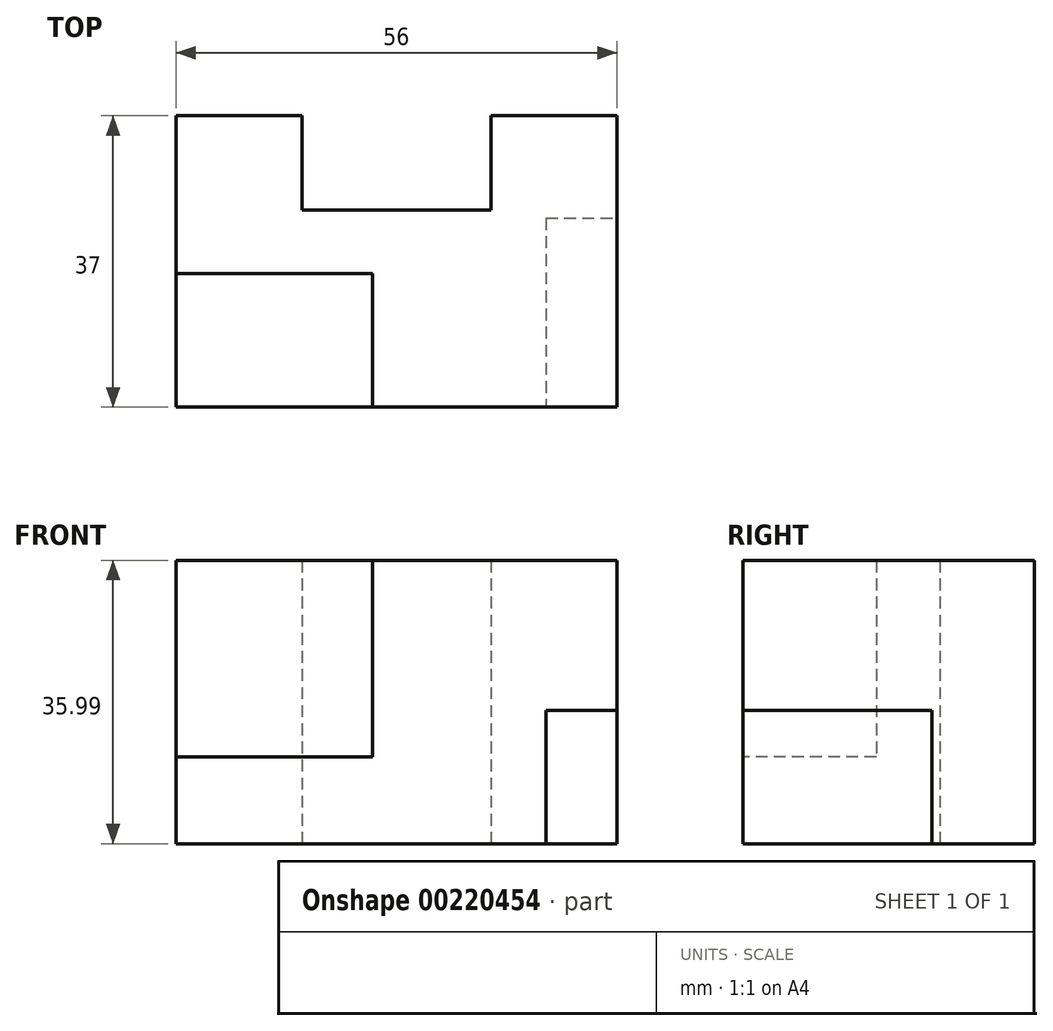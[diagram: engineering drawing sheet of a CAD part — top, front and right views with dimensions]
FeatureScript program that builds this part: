
annotation { "Feature Type Name" : "Feature", "Feature Type Description" : "" }
export const myFeature = defineFeature(function(context is Context, id is Id, definition is map)
    precondition{}
    {
        {
            var Q0;
            Q0=qCreatedBy(makeId("Top.planeOp"),FACE);
            var sketch = newSketch(context, id + "F0", { "sketchPlane" : qUnion([Q0])});
            skLineSegment(sketch, "E0.bottom", {"start": v(28, 18.5) * mm, "end": v(12, 18.5) * mm});
            skLineSegment(sketch, "E0.top", {"start": v(28, -18.5) * mm, "end": v(-28, -18.5) * mm});
            skLineSegment(sketch, "E0.left", {"start": v(28, 18.5) * mm, "end": v(28, -18.5) * mm});
            skLineSegment(sketch, "E0.right", {"start": v(-28, 18.5) * mm, "end": v(-28, -18.5) * mm});
            skPoint(sketch, "E0.middle", {"position": v(0, 0) * mm});
            skLineSegment(sketch, "E1.0", {"start": v(12, 18.5) * mm, "end": v(12, 6.52) * mm});
            skLineSegment(sketch, "E2.0", {"start": v(12, 6.52) * mm, "end": v(-12, 6.52) * mm});
            skLineSegment(sketch, "E3.0", {"start": v(-12, 18.5) * mm, "end": v(-12, 6.52) * mm});
            skLineSegment(sketch, "E4.trimOffspring", {"start": v(-12, 18.5) * mm, "end": v(-28, 18.5) * mm});
            skSolve(sketch);
        }
        {
            var Q0;
            Q0=makeQuery(id+"F0.imprint","IMPRINT",FACE,{"disambiguationData":[TD([[makeQuery(id+"F0.imprint","IMPRINT",EDGE,{"derivedFrom":sQuery(id+"F0.wireOp",EDGE,"E0.bottom")}),1.0]])]});
            extrude(context, id + "F1", {"entities" : qUnion([Q0]), "depth" : 36 * mm});
        }
        {
            var Q0;
            Q0=makeQuery(id+"F1.opExtrude","SWEPT_FACE",FACE,{"disambiguationData":[OSD([sQuery(id+"F0.wireOp",EDGE,"E0.left")])]});
            var sketch = newSketch(context, id + "F2", { "sketchPlane" : qUnion([Q0])});
            skLineSegment(sketch, "E5.bottom", {"start": v(-18.5, 0) * mm, "end": v(5.5, 0) * mm});
            skLineSegment(sketch, "E5.top", {"start": v(-18.5, 16.94) * mm, "end": v(5.5, 16.94) * mm});
            skLineSegment(sketch, "E5.left", {"start": v(-18.5, 0) * mm, "end": v(-18.5, 16.94) * mm});
            skLineSegment(sketch, "E5.right", {"start": v(5.5, 0) * mm, "end": v(5.5, 16.94) * mm});
            skSolve(sketch);
        }
        {
            var Q0;
            Q0=makeQuery(id+"F2.imprint","IMPRINT",FACE,{"disambiguationData":[TD([[makeQuery(id+"F2.imprint","IMPRINT",EDGE,{"derivedFrom":sQuery(id+"F2.wireOp",EDGE,"E5.bottom")}),-1.0]])]});
            extrude(context, id + "F3", {"entities" : qUnion([Q0]), "operationType" : NewBodyOperationType.REMOVE, "oppositeDirection" : true, "depth" : 9 * mm});
        }
        {
            var Q0;
            Q0=makeQuery(id+"F1.opExtrude","SWEPT_FACE",FACE,{"disambiguationData":[OSD([sQuery(id+"F0.wireOp",EDGE,"E0.top")])]});
            var sketch = newSketch(context, id + "F4", { "sketchPlane" : qUnion([Q0])});
            skLineSegment(sketch, "E6.bottom", {"start": v(-28, 36) * mm, "end": v(-3.04, 36) * mm});
            skLineSegment(sketch, "E6.top", {"start": v(-28, 11.05) * mm, "end": v(-3.04, 11.05) * mm});
            skLineSegment(sketch, "E6.left", {"start": v(-28, 36) * mm, "end": v(-28, 11.05) * mm});
            skLineSegment(sketch, "E6.right", {"start": v(-3.04, 36) * mm, "end": v(-3.04, 11.05) * mm});
            skSolve(sketch);
        }
        {
            var Q0;
            Q0=makeQuery(id+"F4.imprint","IMPRINT",FACE,{"disambiguationData":[TD([[makeQuery(id+"F4.imprint","IMPRINT",EDGE,{"derivedFrom":sQuery(id+"F4.wireOp",EDGE,"E6.bottom")}),1.0]])]});
            extrude(context, id + "F5", {"entities" : qUnion([Q0]), "operationType" : NewBodyOperationType.REMOVE, "oppositeDirection" : true, "depth" : 16.94 * mm});
        }
    });
